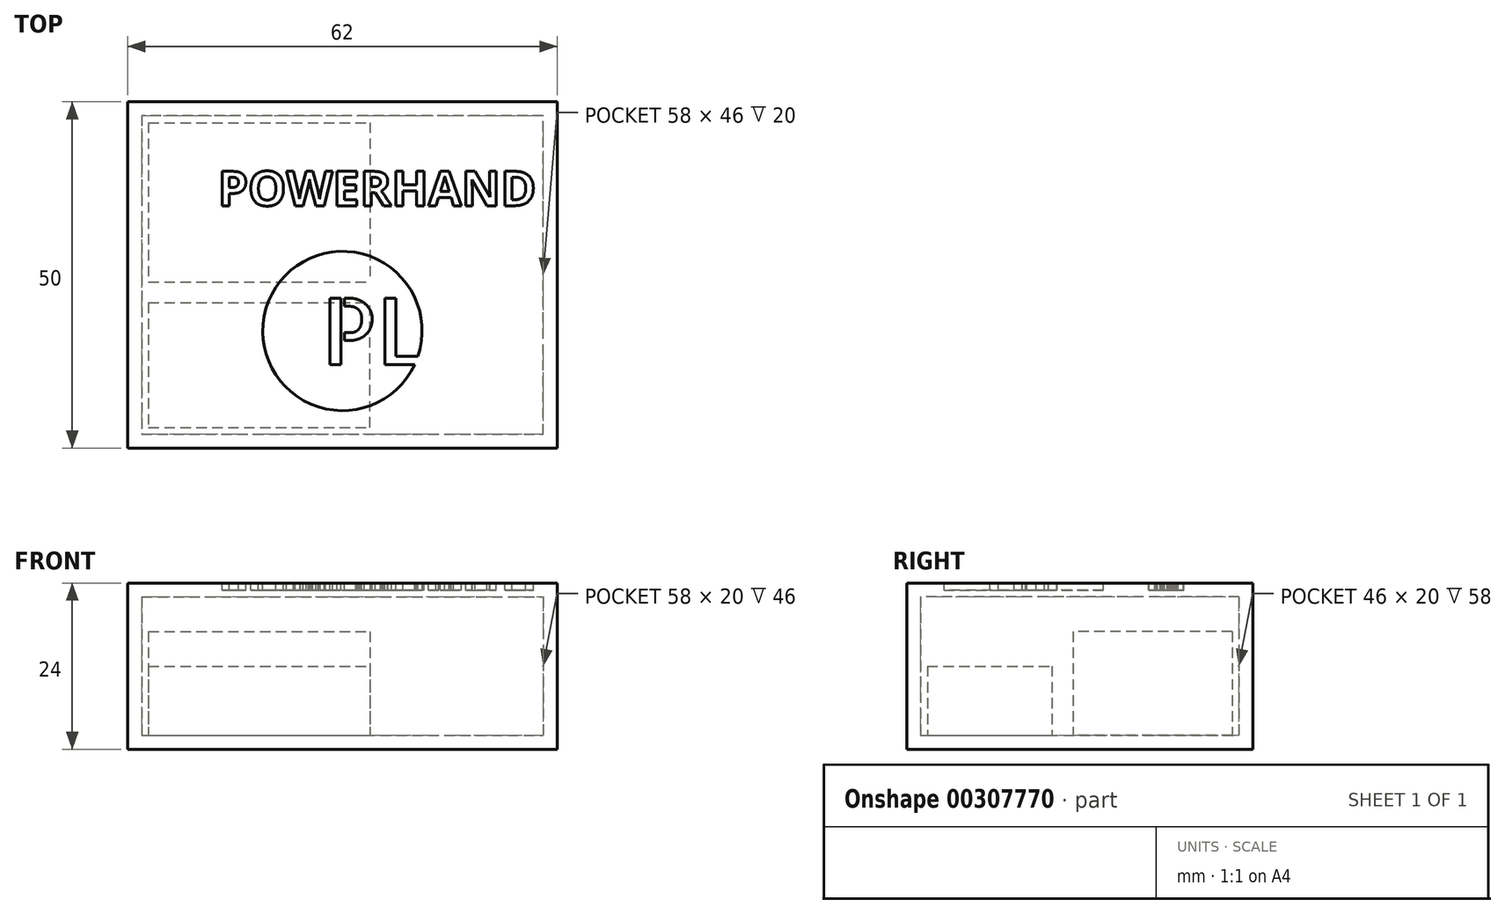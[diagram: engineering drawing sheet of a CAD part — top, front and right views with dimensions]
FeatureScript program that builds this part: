
annotation { "Feature Type Name" : "Feature", "Feature Type Description" : "" }
export const myFeature = defineFeature(function(context is Context, id is Id, definition is map)
    precondition{}
    {
        {
            var Q0;
            Q0=qCreatedBy(makeId("Top.planeOp"),FACE);
            var sketch = newSketch(context, id + "F0", { "sketchPlane" : qUnion([Q0])});
            skLineSegment(sketch, "E0.bottom", {"start": v(-22.66, 4.09) * mm, "end": v(25.34, 4.09) * mm});
            skLineSegment(sketch, "E0.top", {"start": v(-22.66, -13.91) * mm, "end": v(25.34, -13.91) * mm});
            skLineSegment(sketch, "E0.left", {"start": v(-22.66, 4.09) * mm, "end": v(-22.66, -13.91) * mm});
            skLineSegment(sketch, "E0.right", {"start": v(25.34, 4.09) * mm, "end": v(25.34, -13.91) * mm});
            skSolve(sketch);
        }
        {
            var Q0;
            Q0=makeQuery(id+"F0.imprint","IMPRINT",FACE,{"disambiguationData":[TD([[makeQuery(id+"F0.imprint","IMPRINT",EDGE,{"derivedFrom":sQuery(id+"F0.wireOp",EDGE,"E0.bottom")}),-1.0]])]});
            extrude(context, id + "F1", {"entities" : qUnion([Q0]), "depth" : 10 * mm});
        }
        {
            var Q0;
            Q0=makeQuery(id+"F1.opExtrude","CAP_FACE",FACE,{"disambiguationData":[OSD([sQuery(id+"F0.wireOp",EDGE,"E0.bottom"),sQuery(id+"F0.wireOp",EDGE,"E0.top"),sQuery(id+"F0.wireOp",EDGE,"E0.left"),sQuery(id+"F0.wireOp",EDGE,"E0.right")])],"isStart":true});
            var sketch = newSketch(context, id + "F2", { "sketchPlane" : qUnion([Q0])});
            skLineSegment(sketch, "E1.bottom", {"start": v(-22.66, -30.09) * mm, "end": v(17.34, -30.09) * mm});
            skLineSegment(sketch, "E1.top", {"start": v(-22.66, -7.09) * mm, "end": v(17.34, -7.09) * mm});
            skLineSegment(sketch, "E1.left", {"start": v(-22.66, -30.09) * mm, "end": v(-22.66, -7.09) * mm});
            skLineSegment(sketch, "E1.right", {"start": v(17.34, -30.09) * mm, "end": v(17.34, -7.09) * mm});
            skLineSegment(sketch, "E2.0.0", {"start": v(-22.66, -4.09) * mm, "end": v(-22.66, 13.91) * mm});
            skLineSegment(sketch, "E2.0.1", {"start": v(-22.66, 13.91) * mm, "end": v(25.34, 13.91) * mm});
            skLineSegment(sketch, "E2.0.2", {"start": v(25.34, 13.91) * mm, "end": v(25.34, -4.09) * mm});
            skLineSegment(sketch, "E2.0.3", {"start": v(25.34, -4.09) * mm, "end": v(-22.66, -4.09) * mm});
            skSolve(sketch);
        }
        {
            var Q0;
            Q0=makeQuery(id+"F2.imprint","IMPRINT",FACE,{"disambiguationData":[TD([[makeQuery(id+"F2.imprint","IMPRINT",EDGE,{"derivedFrom":sQuery(id+"F2.wireOp",EDGE,"E1.bottom")}),1.0]])]});
            extrude(context, id + "F3", {"entities" : qUnion([Q0]), "oppositeDirection" : true, "depth" : 15 * mm});
        }
        {
            var Q0;
            Q0=makeQuery(id+"F1.opExtrude","CAP_FACE",FACE,{"disambiguationData":[OSD([sQuery(id+"F0.wireOp",EDGE,"E0.bottom"),sQuery(id+"F0.wireOp",EDGE,"E0.top"),sQuery(id+"F0.wireOp",EDGE,"E0.left"),sQuery(id+"F0.wireOp",EDGE,"E0.right")])],"isStart":true});
            var sketch = newSketch(context, id + "F4", { "sketchPlane" : qUnion([Q0])});
            skLineSegment(sketch, "E3.bottom", {"start": v(-25.66, -33.09) * mm, "end": v(34.34, -33.09) * mm});
            skLineSegment(sketch, "E3.top", {"start": v(-25.66, 16.91) * mm, "end": v(34.34, 16.91) * mm});
            skLineSegment(sketch, "E3.left", {"start": v(-25.66, -33.09) * mm, "end": v(-25.66, 16.91) * mm});
            skLineSegment(sketch, "E3.right", {"start": v(34.34, -33.09) * mm, "end": v(34.34, 16.91) * mm});
            skSolve(sketch);
        }
        {
            var Q0;
            Q0=makeQuery(id+"F4.imprint","IMPRINT",FACE,{"disambiguationData":[TD([[makeQuery(id+"F4.imprint","IMPRINT",EDGE,{"derivedFrom":sQuery(id+"F4.wireOp",EDGE,"E3.bottom")}),1.0]])]});
            var Q1;
            Q1=makeQuery(id+"F4.imprint","IMPRINT",FACE,{"disambiguationData":[TD([[makeQuery(id+"F4.imprint","IMPRINT",EDGE,{"derivedFrom":makeQuery(id+"F1.opExtrude","CAP_EDGE",EDGE,{"disambiguationData":[OSD([sQuery(id+"F0.wireOp",EDGE,"E0.bottom")])],"isStart":true})}),1.0]])]});
            extrude(context, id + "F5", {"entities" : qUnion([Q0, Q1]), "depth" : 2 * mm});
        }
        {
            var Q0;
            Q0=makeQuery(id+"F5.opExtrude","CAP_FACE",FACE,{"disambiguationData":[OSD([sQuery(id+"F4.wireOp",EDGE,"E3.bottom"),sQuery(id+"F4.wireOp",EDGE,"E3.top"),sQuery(id+"F4.wireOp",EDGE,"E3.left"),sQuery(id+"F4.wireOp",EDGE,"E3.right")])],"isStart":true});
            var sketch = newSketch(context, id + "F6", { "sketchPlane" : qUnion([Q0])});
            skLineSegment(sketch, "E4.0", {"start": v(-23.66, -14.91) * mm, "end": v(32.34, -14.91) * mm});
            skLineSegment(sketch, "E4.1", {"start": v(-23.66, 31.09) * mm, "end": v(-23.66, -14.91) * mm});
            skLineSegment(sketch, "E4.2", {"start": v(32.34, 31.09) * mm, "end": v(-23.66, 31.09) * mm});
            skLineSegment(sketch, "E4.3", {"start": v(32.34, -14.91) * mm, "end": v(32.34, 31.09) * mm});
            skLineSegment(sketch, "E5.0", {"start": v(-30.66, -21.91) * mm, "end": v(39.34, -21.91) * mm});
            skLineSegment(sketch, "E5.1", {"start": v(-30.66, 38.09) * mm, "end": v(-30.66, -21.91) * mm});
            skLineSegment(sketch, "E5.2", {"start": v(39.34, 38.09) * mm, "end": v(-30.66, 38.09) * mm});
            skLineSegment(sketch, "E5.3", {"start": v(39.34, -21.91) * mm, "end": v(39.34, 38.09) * mm});
            skSolve(sketch);
        }
        {
            var Q0;
            Q0=makeQuery(id+"F6.imprint","IMPRINT",FACE,{"disambiguationData":[TD([[makeQuery(id+"F6.imprint","IMPRINT",EDGE,{"derivedFrom":sQuery(id+"F6.wireOp",EDGE,"E4.0")}),-1.0]])]});
            extrude(context, id + "F7", {"entities" : qUnion([Q0]), "operationType" : NewBodyOperationType.ADD, "depth" : 20 * mm});
        }
        {
            var Q0;
            {var subQ0=sQuery(id+"F4.wireOp",EDGE,"E3.right");Q0=makeQuery(id+"F7.boolean.opBoolean","MERGE",FACE,{"derivedFrom":[makeQuery(id+"F5.opExtrude","SWEPT_FACE",FACE,{"disambiguationData":[OSD([subQ0])]}),makeQuery(id+"F7.opExtrude","SWEPT_FACE",FACE,{"disambiguationData":[OSD([subQ0])]})]});}
            var sketch = newSketch(context, id + "F8", { "sketchPlane" : qUnion([Q0])});
            skLineSegment(sketch, "E6.0.0", {"start": v(-14.91, 0) * mm, "end": v(31.09, 0) * mm});
            skLineSegment(sketch, "E6.0.1", {"start": v(31.09, 0) * mm, "end": v(31.09, 20) * mm});
            skLineSegment(sketch, "E6.0.2", {"start": v(31.09, 20) * mm, "end": v(-14.91, 20) * mm});
            skLineSegment(sketch, "E6.0.3", {"start": v(-14.91, 20) * mm, "end": v(-14.91, 0) * mm});
            skSolve(sketch);
        }
        {
            var Q0;
            Q0=makeQuery(id+"F8.imprint","IMPRINT",FACE,{"disambiguationData":[TD([[makeQuery(id+"F8.imprint","IMPRINT",EDGE,{"derivedFrom":sQuery(id+"F8.wireOp",EDGE,"E6.0.0")}),1.0]])]});
            extrude(context, id + "F9", {"entities" : qUnion([Q0]), "operationType" : NewBodyOperationType.REMOVE, "oppositeDirection" : true, "depth" : 25 * mm});
        }
        {
            var Q0;
            Q0=makeQuery(id+"F7.opExtrude","CAP_FACE",FACE,{"disambiguationData":[OSD([sQuery(id+"F4.wireOp",EDGE,"E3.bottom"),sQuery(id+"F4.wireOp",EDGE,"E3.top"),sQuery(id+"F4.wireOp",EDGE,"E3.left"),sQuery(id+"F4.wireOp",EDGE,"E3.right"),sQuery(id+"F6.wireOp",EDGE,"E4.0"),sQuery(id+"F6.wireOp",EDGE,"E4.1"),sQuery(id+"F6.wireOp",EDGE,"E4.2"),sQuery(id+"F6.wireOp",EDGE,"E4.3")])],"isStart":false});
            var sketch = newSketch(context, id + "F10", { "sketchPlane" : qUnion([Q0])});
            skLineSegment(sketch, "E7.0.0", {"start": v(-23.66, 31.09) * mm, "end": v(34.34, 31.09) * mm});
            skLineSegment(sketch, "E7.0.1", {"start": v(34.34, 31.09) * mm, "end": v(34.34, 33.09) * mm});
            skLineSegment(sketch, "E7.0.2", {"start": v(34.34, 33.09) * mm, "end": v(-25.66, 33.09) * mm});
            skLineSegment(sketch, "E7.0.3", {"start": v(-25.66, 33.09) * mm, "end": v(-25.66, -16.91) * mm});
            skLineSegment(sketch, "E7.0.4", {"start": v(-25.66, -16.91) * mm, "end": v(34.34, -16.91) * mm});
            skLineSegment(sketch, "E7.0.5", {"start": v(34.34, -16.91) * mm, "end": v(34.34, -14.91) * mm});
            skLineSegment(sketch, "E7.0.6", {"start": v(34.34, -14.91) * mm, "end": v(-23.66, -14.91) * mm});
            skLineSegment(sketch, "E7.0.7", {"start": v(-23.66, -14.91) * mm, "end": v(-23.66, 31.09) * mm});
            skLineSegment(sketch, "E8", {"start": v(34.34, 31.09) * mm, "end": v(34.34, -14.91) * mm});
            skSolve(sketch);
        }
        {
            var Q0;
            Q0=makeQuery(id+"F10.imprint","IMPRINT",FACE,{"disambiguationData":[TD([[makeQuery(id+"F10.imprint","IMPRINT",EDGE,{"derivedFrom":sQuery(id+"F10.wireOp",EDGE,"E7.0.0")}),1.0]])]});
            var Q1;
            Q1=makeQuery(id+"F10.imprint","IMPRINT",FACE,{"disambiguationData":[TD([[makeQuery(id+"F10.imprint","IMPRINT",EDGE,{"derivedFrom":sQuery(id+"F10.wireOp",EDGE,"E7.0.0")}),-1.0]])]});
            extrude(context, id + "F11", {"entities" : qUnion([Q0, Q1]), "depth" : 2 * mm});
        }
        {
            var Q0;
            Q0=makeQuery(id+"F11.opExtrude","SWEPT_FACE",FACE,{"disambiguationData":[OSD([sQuery(id+"F10.wireOp",EDGE,"E7.0.1"),sQuery(id+"F10.wireOp",EDGE,"E7.0.5"),sQuery(id+"F10.wireOp",EDGE,"E8")])]});
            var sketch = newSketch(context, id + "F12", { "sketchPlane" : qUnion([Q0])});
            skLineSegment(sketch, "E9.0.0", {"start": v(-14.91, 0) * mm, "end": v(-14.91, 20) * mm});
            skLineSegment(sketch, "E9.0.1", {"start": v(-14.91, 20) * mm, "end": v(-16.91, 20) * mm});
            skLineSegment(sketch, "E9.0.2", {"start": v(-16.91, 20) * mm, "end": v(-16.91, -2) * mm});
            skLineSegment(sketch, "E9.0.3", {"start": v(-16.91, -2) * mm, "end": v(33.09, -2) * mm});
            skLineSegment(sketch, "E9.0.4", {"start": v(33.09, -2) * mm, "end": v(33.09, 20) * mm});
            skLineSegment(sketch, "E9.0.5", {"start": v(33.09, 20) * mm, "end": v(31.09, 20) * mm});
            skLineSegment(sketch, "E9.0.6", {"start": v(31.09, 20) * mm, "end": v(31.09, 0) * mm});
            skLineSegment(sketch, "E9.0.7", {"start": v(31.09, 0) * mm, "end": v(-14.91, 0) * mm});
            skLineSegment(sketch, "E10.0.0", {"start": v(-16.91, 20) * mm, "end": v(33.09, 20) * mm});
            skLineSegment(sketch, "E10.0.1", {"start": v(33.09, 20) * mm, "end": v(33.09, 22) * mm});
            skLineSegment(sketch, "E10.0.2", {"start": v(33.09, 22) * mm, "end": v(-16.91, 22) * mm});
            skLineSegment(sketch, "E10.0.3", {"start": v(-16.91, 22) * mm, "end": v(-16.91, 20) * mm});
            skSolve(sketch);
        }
        {
            var Q0;
            {var subQ2=sQuery(id+"F12.wireOp",EDGE,"E9.0.0");Q0=makeQuery(id+"F12.imprint","IMPRINT",FACE,{"disambiguationData":[TD([[makeQuery(id+"F12.imprint","IMPRINT",EDGE,{"derivedFrom":subQ2}),1.0]])]});}
            var Q1;
            {var subQ0=sQuery(id+"F12.wireOp",EDGE,"E9.0.0");Q1=makeQuery(id+"F12.imprint","IMPRINT",FACE,{"disambiguationData":[TD([[makeQuery(id+"F12.imprint","IMPRINT",EDGE,{"derivedFrom":subQ0}),-1.0]])]});}
            var Q2;
            {var subQ0=sQuery(id+"F12.wireOp",EDGE,"E10.0.1");Q2=makeQuery(id+"F12.imprint","IMPRINT",FACE,{"disambiguationData":[TD([[makeQuery(id+"F12.imprint","IMPRINT",EDGE,{"derivedFrom":subQ0}),-1.0]])]});}
            extrude(context, id + "F13", {"entities" : qUnion([Q0, Q1, Q2]), "operationType" : NewBodyOperationType.ADD, "depth" : 2 * mm});
        }
        {
            var Q0;
            Q0=makeQuery(id+"F13.boolean.opBoolean","MERGE",FACE,{"derivedFrom":[makeQuery(id+"F11.opExtrude","CAP_FACE",FACE,{"disambiguationData":[OSD([sQuery(id+"F10.wireOp",EDGE,"E7.0.1"),sQuery(id+"F10.wireOp",EDGE,"E7.0.2"),sQuery(id+"F10.wireOp",EDGE,"E7.0.3"),sQuery(id+"F10.wireOp",EDGE,"E7.0.4"),sQuery(id+"F10.wireOp",EDGE,"E7.0.5"),sQuery(id+"F10.wireOp",EDGE,"E8")])],"isStart":false}),makeQuery(id+"F13.opExtrude","SWEPT_FACE",FACE,{"disambiguationData":[OSD([sQuery(id+"F12.wireOp",EDGE,"E10.0.2")])]})]});
            var sketch = newSketch(context, id + "F14", { "sketchPlane" : qUnion([Q0])});
            skText(sketch, "E11", { "text": "POWERHAND", "fontName": "OpenSans-Bold.ttf"});
            const initialGuessF14  = {"E11": [-0.01266, 0.01809, 1, 0, 0.005]};
            skSetInitialGuess(sketch, initialGuessF14);
            skSolve(sketch);
        }
        {
            var Q0;
            Q0 = qSketchRegion(id + "F14", true);
            extrude(context, id + "F15", {"entities" : qUnion([Q0]), "operationType" : NewBodyOperationType.REMOVE, "oppositeDirection" : true, "depth" : 1 * mm});
        }
        {
            var Q0;
            {var subQ0=sQuery(id+"F10.wireOp",EDGE,"E7.0.4");var subQ1=sQuery(id+"F10.wireOp",EDGE,"E7.0.3");var subQ5=sQuery(id+"F12.wireOp",EDGE,"E10.0.2");var subQ7=sQuery(id+"F10.wireOp",EDGE,"E7.0.2");Q0=makeQuery(id+"F15.boolean.opBoolean","SPLIT",FACE,{"disambiguationData":[TD([makeQuery(id+"F11.opExtrude","SWEPT_FACE",FACE,{"disambiguationData":[OSD([subQ7])]})])],"derivedFrom":makeQuery(id+"F13.boolean.opBoolean","MERGE",FACE,{"derivedFrom":[makeQuery(id+"F11.opExtrude","CAP_FACE",FACE,{"disambiguationData":[OSD([sQuery(id+"F10.wireOp",EDGE,"E7.0.1"),subQ7,subQ1,subQ0,sQuery(id+"F10.wireOp",EDGE,"E7.0.5"),sQuery(id+"F10.wireOp",EDGE,"E8")])],"isStart":false}),makeQuery(id+"F13.opExtrude","SWEPT_FACE",FACE,{"disambiguationData":[OSD([subQ5])]})]})});}
            var sketch = newSketch(context, id + "F16", { "sketchPlane" : qUnion([Q0])});
            skText(sketch, "E12", { "text": "PL", "fontName": "AllertaStencil-Regular.ttf"});
            skCircle(sketch, "E13", {"center": v(5.34, 0) * mm, "radius": 11.5 * mm});
            const initialGuessF16  = {"E12": [0.00234, -0.00486, 1, 0, 0.00961]};
            skSetInitialGuess(sketch, initialGuessF16);
            skSolve(sketch);
        }
        {
            var Q0;
            Q0=makeQuery(id+"F16.imprint","IMPRINT",FACE,{"disambiguationData":[TD([[makeQuery(id+"F16.imprint","IMPRINT",EDGE,{"derivedFrom":sQuery(id+"F16.wireOp",EDGE,"E12.sketch_text.stroke-0")}),1.0]])]});
            extrude(context, id + "F17", {"entities" : qUnion([Q0]), "operationType" : NewBodyOperationType.REMOVE, "oppositeDirection" : true, "depth" : 1 * mm});
        }
    });
